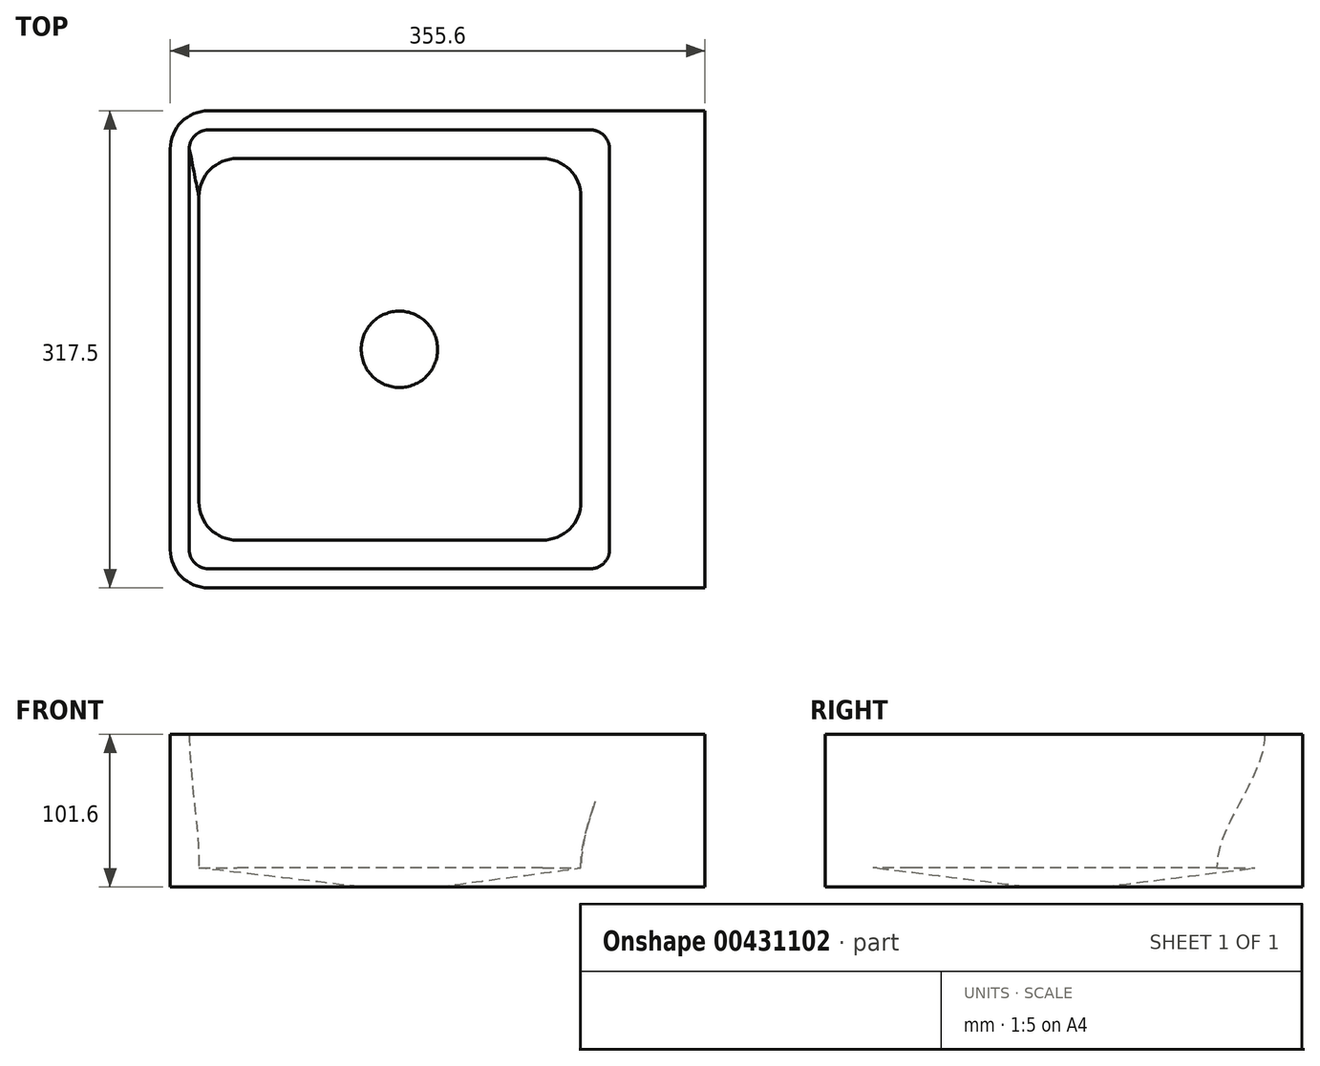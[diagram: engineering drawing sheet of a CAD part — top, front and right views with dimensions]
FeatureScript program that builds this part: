
annotation { "Feature Type Name" : "Feature", "Feature Type Description" : "" }
export const myFeature = defineFeature(function(context is Context, id is Id, definition is map)
    precondition{}
    {
        {
            var Q0;
            Q0=qCreatedBy(makeId("Top.planeOp"),FACE);
            var sketch = newSketch(context, id + "F0", { "sketchPlane" : qUnion([Q0])});
            skLineSegment(sketch, "E0.bottom", {"start": v(-127, 158.75) * mm, "end": v(127, 158.75) * mm});
            skLineSegment(sketch, "E0.top", {"start": v(-127, -158.75) * mm, "end": v(127, -158.75) * mm});
            skLineSegment(sketch, "E0.left", {"start": v(-152.4, 133.35) * mm, "end": v(-152.4, -133.35) * mm});
            skLineSegment(sketch, "E0.right", {"start": v(152.4, 133.35) * mm, "end": v(152.4, -133.35) * mm});
            skPoint(sketch, "E0.middle", {"position": v(0, 0) * mm});
            skPoint(sketch, "E1.visualSharp", {"position": v(-152.4, 158.75) * mm});
            skArc(sketch, "E1.filletArc", {"start": v(-127, 158.75) * mm, "mid": v(-144.96, 151.31) * mm, "end": v(-152.4, 133.35) * mm});
            skPoint(sketch, "E2.visualSharp", {"position": v(152.4, 158.75) * mm});
            skArc(sketch, "E2.filletArc", {"start": v(152.4, 133.35) * mm, "mid": v(144.96, 151.31) * mm, "end": v(127, 158.75) * mm});
            skPoint(sketch, "E3.visualSharp", {"position": v(152.4, -158.75) * mm});
            skArc(sketch, "E3.filletArc", {"start": v(127, -158.75) * mm, "mid": v(144.96, -151.31) * mm, "end": v(152.4, -133.35) * mm});
            skPoint(sketch, "E4.visualSharp", {"position": v(-152.4, -158.75) * mm});
            skArc(sketch, "E4.filletArc", {"start": v(-152.4, -133.35) * mm, "mid": v(-144.96, -151.31) * mm, "end": v(-127, -158.75) * mm});
            skSolve(sketch);
        }
        {
            var Q0;
            Q0 = qSketchRegion(id + "F0", true);
            extrude(context, id + "F1", {"entities" : qUnion([Q0]), "oppositeDirection" : true, "depth" : 101.6 * mm, "offsetDistance" : 25.4 * mm});
        }
        {
            var Q0;
            Q0=makeQuery(id+"F1.opExtrude","CAP_FACE",FACE,{"disambiguationData":[OSD([sQuery(id+"F0.wireOp",EDGE,"E0.bottom"),sQuery(id+"F0.wireOp",EDGE,"E0.top"),sQuery(id+"F0.wireOp",EDGE,"E0.left"),sQuery(id+"F0.wireOp",EDGE,"E0.right"),sQuery(id+"F0.wireOp",EDGE,"E1.filletArc"),sQuery(id+"F0.wireOp",EDGE,"E2.filletArc"),sQuery(id+"F0.wireOp",EDGE,"E3.filletArc"),sQuery(id+"F0.wireOp",EDGE,"E4.filletArc")])],"isStart":true});
            var sketch = newSketch(context, id + "F2", { "sketchPlane" : qUnion([Q0])});
            skLineSegment(sketch, "E5.0", {"start": v(-139.7, 133.35) * mm, "end": v(-139.7, -133.35) * mm});
            skArc(sketch, "E5.1", {"start": v(-127, 146.05) * mm, "mid": v(-135.98, 142.33) * mm, "end": v(-139.7, 133.35) * mm});
            skArc(sketch, "E5.2", {"start": v(-139.7, -133.35) * mm, "mid": v(-135.98, -142.33) * mm, "end": v(-127, -146.05) * mm});
            skLineSegment(sketch, "E5.3", {"start": v(127, 146.05) * mm, "end": v(-127, 146.05) * mm});
            skLineSegment(sketch, "E5.4", {"start": v(-127, -146.05) * mm, "end": v(127, -146.05) * mm});
            skArc(sketch, "E5.5", {"start": v(127, -146.05) * mm, "mid": v(135.98, -142.33) * mm, "end": v(139.7, -133.35) * mm});
            skLineSegment(sketch, "E5.6", {"start": v(139.7, -133.35) * mm, "end": v(139.7, 133.35) * mm});
            skArc(sketch, "E5.7", {"start": v(139.7, 133.35) * mm, "mid": v(135.98, 142.33) * mm, "end": v(127, 146.05) * mm});
            skSolve(sketch);
        }
        {
            var Q0;
            Q0=qCreatedBy(makeId("Top.planeOp"),FACE);
            cPlane(context, id + "F3", {"entities" : qUnion([Q0]), "cplaneType" : CPlaneType.OFFSET, "offset" : 88.9 * mm, "oppositeDirection" : true, "width" : 152.4 * mm, "height" : 152.4 * mm});
        }
        {
            var Q0;
            Q0=qCreatedBy(id+"F3.planeOp",FACE);
            var sketch = newSketch(context, id + "F4", { "sketchPlane" : qUnion([Q0])});
            skLineSegment(sketch, "E6.bottom", {"start": v(95.25, 127) * mm, "end": v(-107.95, 127) * mm});
            skLineSegment(sketch, "E6.top", {"start": v(95.25, -127) * mm, "end": v(-107.95, -127) * mm});
            skLineSegment(sketch, "E6.left", {"start": v(120.65, 101.6) * mm, "end": v(120.65, -101.6) * mm});
            skLineSegment(sketch, "E6.right", {"start": v(-133.35, 101.6) * mm, "end": v(-133.35, -101.6) * mm});
            skPoint(sketch, "E6.middle", {"position": v(0, 0) * mm});
            skPoint(sketch, "E7.visualSharp", {"position": v(-133.35, 127) * mm});
            skArc(sketch, "E7.filletArc", {"start": v(-107.95, 127) * mm, "mid": v(-125.91, 119.56) * mm, "end": v(-133.35, 101.6) * mm});
            skPoint(sketch, "E8.visualSharp", {"position": v(120.65, 127) * mm});
            skArc(sketch, "E8.filletArc", {"start": v(120.65, 101.6) * mm, "mid": v(113.21, 119.56) * mm, "end": v(95.25, 127) * mm});
            skPoint(sketch, "E9.visualSharp", {"position": v(120.65, -127) * mm});
            skArc(sketch, "E9.filletArc", {"start": v(95.25, -127) * mm, "mid": v(113.21, -119.56) * mm, "end": v(120.65, -101.6) * mm});
            skPoint(sketch, "E10.visualSharp", {"position": v(-133.35, -127) * mm});
            skArc(sketch, "E10.filletArc", {"start": v(-133.35, -101.6) * mm, "mid": v(-125.91, -119.56) * mm, "end": v(-107.95, -127) * mm});
            skSolve(sketch);
        }
        {
            var Q1;
            Q1 = qSketchRegion(id + "F2", true);
            var Q2;
            Q2 = qSketchRegion(id + "F4", true);
            loft(context, id + "F5", {"operationType" : NewBodyOperationType.REMOVE, "startCondition" : LoftEndDerivativeType.NORMAL_TO_PROFILE, "startMagnitude" : 1, "endCondition" : LoftEndDerivativeType.NORMAL_TO_PROFILE, "endMagnitude" : 1, "sheetProfilesArray" : [{ "sheetProfileEntities" : qUnion([Q1]) }, { "sheetProfileEntities" : qUnion([Q2]) }]});
        }
        {
            var Q0;
            Q0=qCreatedBy(makeId("Top.planeOp"),FACE);
            cPlane(context, id + "F6", {"entities" : qUnion([Q0]), "cplaneType" : CPlaneType.OFFSET, "offset" : 101.6 * mm, "oppositeDirection" : true, "width" : 152.4 * mm, "height" : 152.4 * mm});
        }
        {
            var Q0;
            Q0=qCreatedBy(id+"F6.planeOp",FACE);
            var sketch = newSketch(context, id + "F7", { "sketchPlane" : qUnion([Q0])});
            skCircle(sketch, "E11", {"center": v(0, 0) * mm, "radius": 25.4 * mm});
            skSolve(sketch);
        }
        {
            var Q1;
            Q1 = qSketchRegion(id + "F7", true);
            var Q2;
            Q2 = qSketchRegion(id + "F4", true);
            loft(context, id + "F8", {"operationType" : NewBodyOperationType.REMOVE, "sheetProfilesArray" : [{ "sheetProfileEntities" : qUnion([Q1]) }, { "sheetProfileEntities" : qUnion([Q2]) }]});
        }
        {
            var Q0;
            Q0=makeQuery(id+"F0.imprint","IMPRINT",FACE,{"disambiguationData":[TD([[makeQuery(id+"F0.imprint","IMPRINT",EDGE,{"derivedFrom":sQuery(id+"F0.wireOp",EDGE,"E0.bottom")}),-1.0]])]});
            var sketch = newSketch(context, id + "F9", { "sketchPlane" : qUnion([Q0])});
            skFitSpline(sketch, "E12.0", {"points": [v(127, 146.05) * mm, v(127.83, 146.05) * mm, v(128.66, 145.97) * mm, v(129.48, 145.8) * mm, v(130.3, 145.64) * mm, v(131.1, 145.4) * mm, v(131.86, 145.08) * mm, v(132.63, 144.76) * mm, v(133.36, 144.37) * mm, v(134.06, 143.9) * mm, v(134.75, 143.45) * mm, v(135.4, 142.92) * mm, v(135.98, 142.33) * mm, v(136.57, 141.74) * mm, v(137.1, 141.1) * mm, v(137.56, 140.4) * mm, v(138.02, 139.71) * mm, v(138.41, 138.98) * mm, v(138.73, 138.21) * mm, v(139.05, 137.44) * mm, v(139.3, 136.65) * mm, v(139.46, 135.83) * mm, v(139.62, 135) * mm, v(139.7, 134.18) * mm, v(139.7, 133.35) * mm]});
            skFitSpline(sketch, "E12.1", {"points": [v(139.7, 133.35) * mm, v(139.7, 44.45) * mm, v(139.7, -44.45) * mm, v(139.7, -133.35) * mm]});
            skFitSpline(sketch, "E12.2", {"points": [v(139.7, -133.35) * mm, v(139.7, -134.18) * mm, v(139.62, -135) * mm, v(139.46, -135.83) * mm, v(139.3, -136.65) * mm, v(139.05, -137.44) * mm, v(138.73, -138.21) * mm, v(138.41, -138.98) * mm, v(138.02, -139.71) * mm, v(137.56, -140.4) * mm, v(137.1, -141.1) * mm, v(136.57, -141.74) * mm, v(135.98, -142.33) * mm, v(135.4, -142.92) * mm, v(134.75, -143.45) * mm, v(134.06, -143.9) * mm, v(133.36, -144.37) * mm, v(132.63, -144.76) * mm, v(131.86, -145.08) * mm, v(131.09, -145.4) * mm, v(130.3, -145.64) * mm, v(129.48, -145.8) * mm, v(128.66, -145.97) * mm, v(127.83, -146.05) * mm, v(127, -146.05) * mm]});
            skLineSegment(sketch, "E13", {"start": v(127, -146.05) * mm, "end": v(127, -158.75) * mm});
            skLineSegment(sketch, "E14", {"start": v(127, -158.75) * mm, "end": v(203.2, -158.75) * mm});
            skLineSegment(sketch, "E15", {"start": v(203.2, -158.75) * mm, "end": v(203.2, 158.75) * mm});
            skLineSegment(sketch, "E16", {"start": v(203.2, 158.75) * mm, "end": v(127, 158.75) * mm});
            skLineSegment(sketch, "E17", {"start": v(127, 158.75) * mm, "end": v(127, 146.05) * mm});
            skSolve(sketch);
        }
        {
            var Q0;
            Q0 = qSketchRegion(id + "F9", true);
            extrude(context, id + "F10", {"entities" : qUnion([Q0]), "operationType" : NewBodyOperationType.ADD, "oppositeDirection" : true, "depth" : 101.6 * mm, "offsetDistance" : 25.4 * mm});
        }
    });
